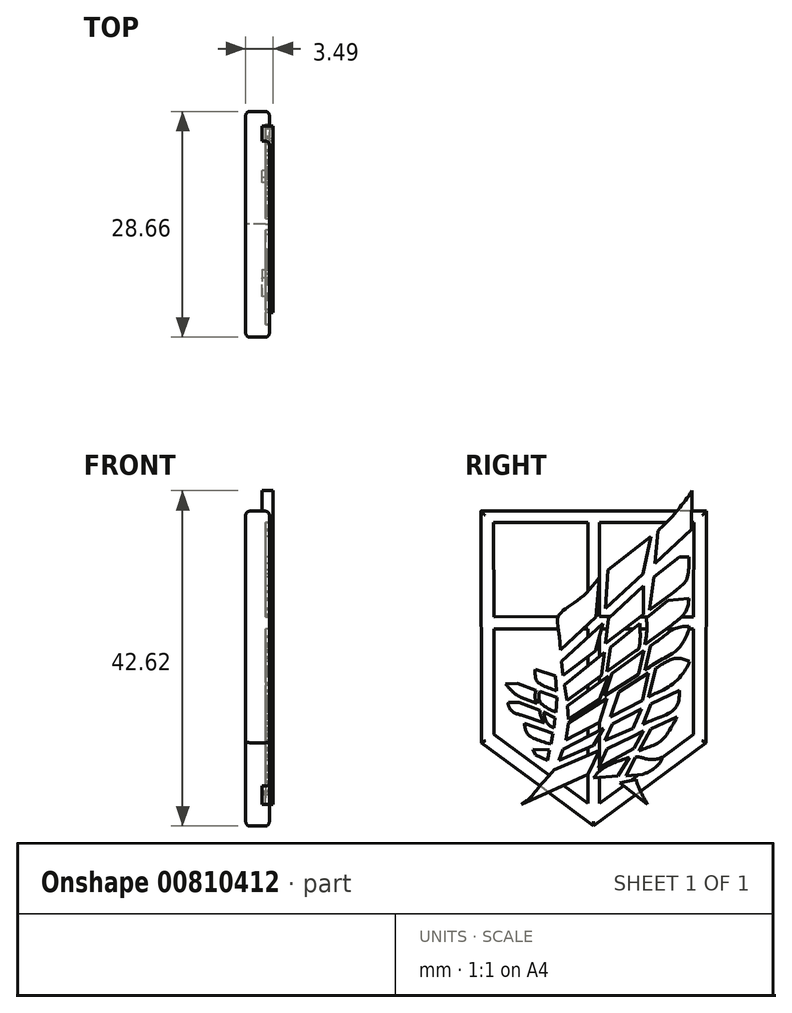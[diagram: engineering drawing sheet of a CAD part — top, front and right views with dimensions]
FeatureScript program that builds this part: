
annotation { "Feature Type Name" : "Feature", "Feature Type Description" : "" }
export const myFeature = defineFeature(function(context is Context, id is Id, definition is map)
    precondition{}
    {
        {
            var Q0;
            Q0=qCreatedBy(makeId("Right.planeOp"),FACE);
            var sketch = newSketch(context, id + "F0", { "sketchPlane" : qUnion([Q0])});
            skLineSegment(sketch, "E0.top", {"start": v(14.33, 19.11) * mm, "end": v(-14.33, 19.11) * mm});
            skPoint(sketch, "E0.middle", {"position": v(0, 0) * mm});
            skLineSegment(sketch, "E1", {"start": v(0, -20.89) * mm, "end": v(-14.26, -10.3) * mm});
            skLineSegment(sketch, "E2", {"start": v(0, 19.11) * mm, "end": v(0, -20.89) * mm, "construction": true});
            skLineSegment(sketch, "E3.MirrorCS", {"start": v(0, -20.89) * mm, "end": v(14.26, -10.3) * mm});
            skLineSegment(sketch, "E4", {"start": v(-14.33, 19.11) * mm, "end": v(-14.26, -10.3) * mm});
            skLineSegment(sketch, "E5", {"start": v(14.33, 19.11) * mm, "end": v(14.26, -10.3) * mm});
            skSolve(sketch);
        }
        {
            var Q0;
            Q0 = qSketchRegion(id + "F0", true);
            extrude(context, id + "F1", {"entities" : qUnion([Q0]), "depth" : 3 * mm, "offsetDistance" : 25 * mm});
        }
        {
            var Q0;
            Q0=makeQuery(id+"F1.opExtrude","CAP_EDGE",EDGE,{"disambiguationData":[OSD([sQuery(id+"F0.wireOp",EDGE,"E4")])],"isStart":false});
            var Q1;
            Q1=makeQuery(id+"F1.opExtrude","CAP_EDGE",EDGE,{"disambiguationData":[OSD([sQuery(id+"F0.wireOp",EDGE,"E0.top")])],"isStart":false});
            var Q2;
            Q2=makeQuery(id+"F1.opExtrude","CAP_EDGE",EDGE,{"disambiguationData":[OSD([sQuery(id+"F0.wireOp",EDGE,"E5")])],"isStart":false});
            var Q3;
            Q3=makeQuery(id+"F1.opExtrude","CAP_EDGE",EDGE,{"disambiguationData":[OSD([sQuery(id+"F0.wireOp",EDGE,"E3.MirrorCS")])],"isStart":false});
            var Q4;
            Q4=makeQuery(id+"F1.opExtrude","CAP_EDGE",EDGE,{"disambiguationData":[OSD([sQuery(id+"F0.wireOp",EDGE,"E1")])],"isStart":false});
            fillet(context, id + "F2", {"entities" : qUnion([Q0, Q1, Q2, Q3, Q4]), "radius" : 0.5 * mm, "tangentPropagation" : true, "allowEdgeOverflow" : false});
        }
        {
            var Q0;
            Q0=makeQuery(id+"F1.opExtrude","CAP_EDGE",EDGE,{"disambiguationData":[OSD([sQuery(id+"F0.wireOp",EDGE,"E5")])],"isStart":true});
            var Q1;
            Q1=makeQuery(id+"F1.opExtrude","CAP_EDGE",EDGE,{"disambiguationData":[OSD([sQuery(id+"F0.wireOp",EDGE,"E3.MirrorCS")])],"isStart":true});
            var Q2;
            Q2=makeQuery(id+"F1.opExtrude","CAP_EDGE",EDGE,{"disambiguationData":[OSD([sQuery(id+"F0.wireOp",EDGE,"E1")])],"isStart":true});
            var Q3;
            Q3=makeQuery(id+"F1.opExtrude","CAP_EDGE",EDGE,{"disambiguationData":[OSD([sQuery(id+"F0.wireOp",EDGE,"E4")])],"isStart":true});
            var Q4;
            Q4=makeQuery(id+"F1.opExtrude","CAP_EDGE",EDGE,{"disambiguationData":[OSD([sQuery(id+"F0.wireOp",EDGE,"E0.top")])],"isStart":true});
            fillet(context, id + "F3", {"entities" : qUnion([Q0, Q1, Q2, Q3, Q4]), "radius" : 0.5 * mm, "tangentPropagation" : true, "allowEdgeOverflow" : false});
        }
        {
            var Q0;
            Q0=makeQuery(id+"F1.opExtrude","CAP_FACE",FACE,{"disambiguationData":[OSD([sQuery(id+"F0.wireOp",EDGE,"E0.top"),sQuery(id+"F0.wireOp",EDGE,"E1"),sQuery(id+"F0.wireOp",EDGE,"E3.MirrorCS"),sQuery(id+"F0.wireOp",EDGE,"E4"),sQuery(id+"F0.wireOp",EDGE,"E5")])],"isStart":false});
            var sketch = newSketch(context, id + "F4", { "sketchPlane" : qUnion([Q0])});
            skLineSegment(sketch, "E6", {"start": v(0, 18.61) * mm, "end": v(-13.83, 18.61) * mm});
            skLineSegment(sketch, "E7", {"start": v(-13.83, 18.61) * mm, "end": v(-13.76, -10.04) * mm});
            skLineSegment(sketch, "E8", {"start": v(-13.76, -10.04) * mm, "end": v(0, -20.27) * mm});
            skLineSegment(sketch, "E9", {"start": v(0, -20.27) * mm, "end": v(13.76, -10.04) * mm});
            skLineSegment(sketch, "E10", {"start": v(13.76, -10.04) * mm, "end": v(13.83, 18.61) * mm});
            skLineSegment(sketch, "E11", {"start": v(13.83, 18.61) * mm, "end": v(0, 18.61) * mm});
            skLineSegment(sketch, "E12", {"start": v(0, 18.61) * mm, "end": v(0, -20.27) * mm});
            skLineSegment(sketch, "E13", {"start": v(-12.7, 4.17) * mm, "end": v(-12.7, -9.22) * mm});
            skLineSegment(sketch, "E14", {"start": v(-12.7, -9.22) * mm, "end": v(-0.75, -18.02) * mm});
            skLineSegment(sketch, "E15", {"start": v(-0.75, -18.02) * mm, "end": v(-0.75, 4.17) * mm});
            skLineSegment(sketch, "E16", {"start": v(-0.75, 4.17) * mm, "end": v(-12.7, 4.17) * mm});
            skLineSegment(sketch, "E17", {"start": v(-12.75, 17.67) * mm, "end": v(-12.7, 5.67) * mm});
            skLineSegment(sketch, "E18", {"start": v(-12.7, 5.67) * mm, "end": v(-0.76, 5.73) * mm});
            skLineSegment(sketch, "E19", {"start": v(-0.76, 5.73) * mm, "end": v(-0.75, 17.7) * mm});
            skLineSegment(sketch, "E20", {"start": v(-0.75, 17.7) * mm, "end": v(-12.75, 17.67) * mm});
            skLineSegment(sketch, "E21.MirrorCS", {"start": v(0.76, 5.73) * mm, "end": v(0.75, 17.7) * mm});
            skLineSegment(sketch, "E22.MirrorCS", {"start": v(0.75, 17.7) * mm, "end": v(12.75, 17.67) * mm});
            skLineSegment(sketch, "E23.MirrorCS", {"start": v(12.75, 17.67) * mm, "end": v(12.7, 5.67) * mm});
            skLineSegment(sketch, "E24.MirrorCS", {"start": v(12.7, 5.67) * mm, "end": v(0.76, 5.73) * mm});
            skLineSegment(sketch, "E25.MirrorCS", {"start": v(0.75, -18.02) * mm, "end": v(0.75, 4.17) * mm});
            skLineSegment(sketch, "E26.MirrorCS", {"start": v(0.75, 4.17) * mm, "end": v(12.7, 4.17) * mm});
            skLineSegment(sketch, "E27.MirrorCS", {"start": v(12.7, -9.22) * mm, "end": v(0.75, -18.02) * mm});
            skLineSegment(sketch, "E28.MirrorCS", {"start": v(12.7, 4.17) * mm, "end": v(12.7, -9.22) * mm});
            skSolve(sketch);
        }
        {
            var Q0;
            Q0=makeQuery(id+"F4.imprint","IMPRINT",FACE,{"disambiguationData":[TD([[makeQuery(id+"F4.imprint","IMPRINT",EDGE,{"derivedFrom":sQuery(id+"F4.wireOp",EDGE,"E17")}),1.0]])]});
            var Q1;
            Q1=makeQuery(id+"F4.imprint","IMPRINT",FACE,{"disambiguationData":[TD([[makeQuery(id+"F4.imprint","IMPRINT",EDGE,{"derivedFrom":sQuery(id+"F4.wireOp",EDGE,"E13")}),1.0]])]});
            var Q2;
            Q2=makeQuery(id+"F4.imprint","IMPRINT",FACE,{"disambiguationData":[TD([[makeQuery(id+"F4.imprint","IMPRINT",EDGE,{"derivedFrom":sQuery(id+"F4.wireOp",EDGE,"E21.MirrorCS")}),-1.0]])]});
            var Q3;
            Q3=makeQuery(id+"F4.imprint","IMPRINT",FACE,{"disambiguationData":[TD([[makeQuery(id+"F4.imprint","IMPRINT",EDGE,{"derivedFrom":sQuery(id+"F4.wireOp",EDGE,"E25.MirrorCS")}),-1.0]])]});
            extrude(context, id + "F5", {"entities" : qUnion([Q0, Q1, Q2, Q3]), "operationType" : NewBodyOperationType.REMOVE, "oppositeDirection" : true, "depth" : 0.49 * mm, "offsetDistance" : 25 * mm});
        }
        {
            var Q0;
            Q0=makeQuery(id+"F1.opExtrude","CAP_FACE",FACE,{"disambiguationData":[OSD([sQuery(id+"F0.wireOp",EDGE,"E0.top"),sQuery(id+"F0.wireOp",EDGE,"E1"),sQuery(id+"F0.wireOp",EDGE,"E3.MirrorCS"),sQuery(id+"F0.wireOp",EDGE,"E4"),sQuery(id+"F0.wireOp",EDGE,"E5")])],"isStart":false});
            var sketch = newSketch(context, id + "F6", { "sketchPlane" : qUnion([Q0])});
            skLineSegment(sketch, "E29", {"start": v(-0.75, -14.35) * mm, "end": v(-9.17, -18.12) * mm});
            skFitSpline(sketch, "E30", {"points": [v(-9.17, -18.12) * mm, v(-8.07, -17.3) * mm, v(-6.52, -15.42) * mm, v(-5.07, -13.75) * mm], "startDerivative": vector(5.46, 4.28) * mm, "endDerivative": vector(4.45, 5.93) * mm});
            skPoint(sketch, "E31", {"position": v(-7.12, -16.16) * mm});
            skLineSegment(sketch, "E32", {"start": v(-0.75, -14.35) * mm, "end": v(0.75, -11.27) * mm});
            skLineSegment(sketch, "E33", {"start": v(0.75, -11.27) * mm, "end": v(-5.07, -13.75) * mm});
            skLineSegment(sketch, "E34", {"start": v(0.6, -13.5) * mm, "end": v(1.69, -11.1) * mm});
            skLineSegment(sketch, "E35", {"start": v(1.69, -11.1) * mm, "end": v(4.98, -9.52) * mm});
            skLineSegment(sketch, "E36", {"start": v(0.6, -13.5) * mm, "end": v(5.09, -11.04) * mm});
            skLineSegment(sketch, "E37", {"start": v(5.09, -11.04) * mm, "end": v(6.3, -8.8) * mm});
            skLineSegment(sketch, "E38", {"start": v(6.3, -8.8) * mm, "end": v(4.98, -9.52) * mm});
            skLineSegment(sketch, "E39", {"start": v(7.29, -8.53) * mm, "end": v(5.77, -11.32) * mm});
            skLineSegment(sketch, "E40", {"start": v(7.29, -8.53) * mm, "end": v(10.58, -7.01) * mm});
            skFitSpline(sketch, "E41", {"points": [v(5.77, -11.32) * mm, v(8.5, -10.1) * mm, v(10.58, -7.01) * mm], "startDerivative": vector(6.29, 2.79) * mm, "endDerivative": vector(3.58, 6.64) * mm});
            skLineSegment(sketch, "E42", {"start": v(0, -14.79) * mm, "end": v(3.1, -14.5) * mm});
            skLineSegment(sketch, "E43", {"start": v(3.1, -14.5) * mm, "end": v(4.52, -12.17) * mm});
            skPoint(sketch, "E44.3.internal.snap0", {"position": v(2.84, -12.27) * mm});
            skPoint(sketch, "E45", {"position": v(2.26, -13.48) * mm});
            skFitSpline(sketch, "E46", {"points": [v(0, -14.79) * mm, v(0.75, -13.9) * mm, v(2.26, -13) * mm, v(4.52, -12.17) * mm], "startDerivative": vector(2.4, 3.4) * mm, "endDerivative": vector(5.99, 1.99) * mm});
            skPoint(sketch, "E47.1.internal.snap0", {"position": v(3.8, -13.34) * mm});
            skLineSegment(sketch, "E48", {"start": v(4.1, -14.5) * mm, "end": v(5.28, -12.14) * mm});
            skPoint(sketch, "E49.1.internal.snap0", {"position": v(6.72, -13.62) * mm});
            skPoint(sketch, "E49.4.internal.snap0", {"position": v(6.88, -15.15) * mm});
            skFitSpline(sketch, "E50", {"points": [v(5.28, -12.14) * mm, v(5.89, -12.14) * mm, v(6.64, -12.36) * mm, v(7.91, -12.4) * mm, v(8.73, -12.14) * mm], "startDerivative": vector(2.9, 0.26) * mm, "endDerivative": vector(3, 1.23) * mm});
            skFitSpline(sketch, "E51", {"points": [v(8.73, -12.14) * mm, v(8.48, -12.72) * mm, v(7.74, -13.52) * mm, v(6.7, -14.14) * mm, v(6.23, -14.3) * mm], "startDerivative": vector(-0.9, -2.6) * mm, "endDerivative": vector(-2.16, -0.6) * mm});
            skLineSegment(sketch, "E52", {"start": v(4.1, -14.5) * mm, "end": v(6.23, -14.3) * mm});
            skLineSegment(sketch, "E53", {"start": v(5.4, -14.99) * mm, "end": v(3.31, -15.42) * mm});
            skPoint(sketch, "E54.2.internal.snap0", {"position": v(4.36, -15.2) * mm});
            skLineSegment(sketch, "E55", {"start": v(-9.17, -18.12) * mm, "end": v(11.05, -18.12) * mm, "construction": true});
            skLineSegment(sketch, "E56", {"start": v(3.31, -15.42) * mm, "end": v(6.85, -18.12) * mm});
            skFitSpline(sketch, "E57", {"points": [v(5.4, -14.99) * mm, v(5.48, -15.29) * mm, v(5.67, -15.83) * mm, v(5.93, -16.46) * mm, v(6.16, -16.9) * mm, v(6.6, -17.69) * mm, v(6.85, -18.12) * mm], "startDerivative": vector(0.75, -2.31) * mm, "endDerivative": vector(1.42, -2.48) * mm});
            skFitSpline(sketch, "E58", {"points": [v(-5.07, -13.75) * mm, v(-4.19, -11.96) * mm, v(-3.23, -7.81) * mm, v(-4, -0.95) * mm, v(-4.64, 5.71) * mm], "startDerivative": vector(5.68, 9.91) * mm, "endDerivative": vector(-3.76, 21.86) * mm, "construction": true});
            skLineSegment(sketch, "E59", {"start": v(-3.88, -11.13) * mm, "end": v(-4.44, -12.54) * mm});
            skFitSpline(sketch, "E60", {"points": [v(-4.64, 5.71) * mm, v(-4.64, 6.7) * mm, v(-2.24, 8.4) * mm, v(2.56, 12.25) * mm, v(9.26, 17.68) * mm, v(12.46, 21.73) * mm, v(12.48, 21.9) * mm], "startDerivative": vector(-2.87, 11.45) * mm, "endDerivative": vector(-0.94, 2.56) * mm, "construction": true});
            skFitSpline(sketch, "E61", {"points": [v(10.58, -7.01) * mm, v(11.67, -2.07) * mm, v(13.34, 6.4) * mm, v(12.46, 21.73) * mm], "startDerivative": vector(3.82, 19.04) * mm, "endDerivative": vector(-4.27, 37.96) * mm, "construction": true});
            skPoint(sketch, "E62.0.internal.snap0", {"position": v(-6.72, -13.62) * mm});
            skPoint(sketch, "E62.2.internal.snap0", {"position": v(-4.96, -16.24) * mm});
            skPoint(sketch, "E62.3.internal.snap0", {"position": v(-4.96, -16.24) * mm});
            skPoint(sketch, "E62.4.internal.snap0", {"position": v(-6.72, -13.62) * mm});
            skFitSpline(sketch, "E62", {"points": [v(-6.15, -13.62) * mm, v(-5.6, -11.2) * mm, v(-4.96, -7.66) * mm, v(-4.96, -1.26) * mm, v(-6.72, 5.7) * mm, v(-5.6, 7.98) * mm, v(-1.64, 10.32) * mm], "startDerivative": vector(5.06, 18.87) * mm, "endDerivative": vector(25.42, 13.57) * mm, "construction": true});
            skFitSpline(sketch, "E63", {"points": [v(-11.36, 20.74) * mm, v(-8.65, 20.1) * mm, v(-2.94, 16) * mm, v(-1.64, 10.32) * mm], "startDerivative": vector(9.6, -1.22) * mm, "endDerivative": vector(0.23, -16.78) * mm, "construction": true});
            skFitSpline(sketch, "E64", {"points": [v(-12.28, 9.15) * mm, v(-12.72, 11.67) * mm, v(-12.73, 14.4) * mm, v(-11.36, 20.74) * mm], "startDerivative": vector(-1.84, 9.3) * mm, "endDerivative": vector(4.02, 15.96) * mm, "construction": true});
            skLineSegment(sketch, "E65", {"start": v(1.22, -8.5) * mm, "end": v(0, -10.63) * mm});
            skLineSegment(sketch, "E66", {"start": v(0, -10.63) * mm, "end": v(-4.44, -12.54) * mm});
            skLineSegment(sketch, "E67", {"start": v(-3.88, -11.13) * mm, "end": v(1.22, -8.5) * mm});
            skLineSegment(sketch, "E68", {"start": v(1.43, -10.02) * mm, "end": v(2.38, -7.92) * mm});
            skLineSegment(sketch, "E69", {"start": v(2.38, -7.92) * mm, "end": v(6.1, -6) * mm});
            skLineSegment(sketch, "E70", {"start": v(6.1, -6) * mm, "end": v(4.97, -8.5) * mm});
            skLineSegment(sketch, "E71", {"start": v(4.97, -8.5) * mm, "end": v(1.43, -10.02) * mm});
            skLineSegment(sketch, "E72", {"start": v(7.3, -5.39) * mm, "end": v(6.24, -7.96) * mm});
            skFitSpline(sketch, "E73", {"points": [v(6.24, -7.96) * mm, v(7.73, -7.31) * mm, v(9.8, -6.43) * mm, v(10.68, -5.37) * mm, v(10.9, -3.66) * mm], "startDerivative": vector(5.71, 2.62) * mm, "endDerivative": vector(0.28, 7.35) * mm});
            skFitSpline(sketch, "E74", {"points": [v(7.3, -5.39) * mm, v(10.9, -3.66) * mm], "startDerivative": vector(3.6, 1.73) * mm, "endDerivative": vector(3.6, 1.73) * mm});
            skLineSegment(sketch, "E75", {"start": v(-3.53, -9.95) * mm, "end": v(-3.23, -7.81) * mm});
            skLineSegment(sketch, "E76", {"start": v(1.71, -4.7) * mm, "end": v(0.75, -7.73) * mm});
            skPoint(sketch, "E76.endSnap0", {"position": v(0.75, -6.92) * mm});
            skLineSegment(sketch, "E77", {"start": v(0.75, -7.73) * mm, "end": v(-3.53, -9.95) * mm});
            skLineSegment(sketch, "E78", {"start": v(-3.23, -7.81) * mm, "end": v(1.71, -4.7) * mm});
            skLineSegment(sketch, "E79", {"start": v(2.15, -7) * mm, "end": v(3.2, -3.86) * mm});
            skPoint(sketch, "E79.endSnap0", {"position": v(3.2, -9.26) * mm});
            skLineSegment(sketch, "E80", {"start": v(3.2, -3.86) * mm, "end": v(6.94, -1.45) * mm});
            skLineSegment(sketch, "E81", {"start": v(6.94, -1.45) * mm, "end": v(6.2, -4.9) * mm});
            skLineSegment(sketch, "E82", {"start": v(6.2, -4.9) * mm, "end": v(2.15, -7) * mm});
            skLineSegment(sketch, "E83", {"start": v(7.94, -0.83) * mm, "end": v(6.94, -4.52) * mm});
            skFitSpline(sketch, "E84", {"points": [v(6.94, -4.52) * mm, v(7.98, -3.98) * mm, v(9.72, -3.08) * mm, v(11.43, -1.35) * mm, v(12.2, 0) * mm], "startDerivative": vector(4.71, 2.6) * mm, "endDerivative": vector(2.67, 5.56) * mm});
            skFitSpline(sketch, "E85", {"points": [v(7.94, -0.83) * mm, v(9.26, 0) * mm, v(10.77, 0.43) * mm, v(12.2, 0) * mm], "startDerivative": vector(3.8, 2.6) * mm, "endDerivative": vector(4.26, -1.94) * mm});
            skLineSegment(sketch, "E86", {"start": v(0.75, -4.8) * mm, "end": v(1.9, -1.82) * mm});
            skLineSegment(sketch, "E87", {"start": v(-3.34, -5.6) * mm, "end": v(1.9, -1.82) * mm});
            skLineSegment(sketch, "E88", {"start": v(-3.34, -5.6) * mm, "end": v(-3.23, -7.35) * mm});
            skLineSegment(sketch, "E89", {"start": v(1.39, -4.38) * mm, "end": v(2.34, -1.5) * mm});
            skLineSegment(sketch, "E90", {"start": v(6.42, 1.43) * mm, "end": v(5.7, -1.6) * mm});
            skLineSegment(sketch, "E91", {"start": v(1.39, -4.38) * mm, "end": v(5.7, -1.6) * mm});
            skLineSegment(sketch, "E92", {"start": v(2.34, -1.5) * mm, "end": v(6.42, 1.43) * mm});
            skLineSegment(sketch, "E93", {"start": v(6.5, -1.09) * mm, "end": v(7.23, 2.01) * mm});
            skFitSpline(sketch, "E94", {"points": [v(6.5, -1.09) * mm, v(8.62, 0.28) * mm, v(10.78, 1.67) * mm, v(12.11, 4.17) * mm, v(12.11, 4.52) * mm], "startDerivative": vector(7.17, 5.06) * mm, "endDerivative": vector(-0.5, 2.4) * mm});
            skFitSpline(sketch, "E95", {"points": [v(7.23, 2.01) * mm, v(9.02, 3.3) * mm, v(10.24, 4.17) * mm, v(12.11, 4.52) * mm], "startDerivative": vector(5.28, 3.6) * mm, "endDerivative": vector(6.03, 0.55) * mm});
            skLineSegment(sketch, "E96", {"start": v(-3.43, -4.9) * mm, "end": v(-3.72, -2.98) * mm});
            skLineSegment(sketch, "E97", {"start": v(-3.72, -2.98) * mm, "end": v(1.37, 1.18) * mm});
            skLineSegment(sketch, "E98", {"start": v(1.37, 1.18) * mm, "end": v(1, -1.75) * mm});
            skLineSegment(sketch, "E99", {"start": v(1, -1.75) * mm, "end": v(-3.43, -4.9) * mm});
            skLineSegment(sketch, "E100", {"start": v(1.68, -1.26) * mm, "end": v(2.15, 1.83) * mm});
            skLineSegment(sketch, "E101", {"start": v(-3.23, -7.35) * mm, "end": v(0.75, -4.8) * mm});
            skLineSegment(sketch, "E102", {"start": v(1.68, -1.26) * mm, "end": v(5.33, 1.37) * mm});
            skLineSegment(sketch, "E103", {"start": v(5.86, 4.85) * mm, "end": v(2.15, 1.83) * mm});
            skFitSpline(sketch, "E104", {"points": [v(5.33, 1.37) * mm, v(5.65, 1.6) * mm, v(5.9, 2.5) * mm, v(5.86, 4.85) * mm], "startDerivative": vector(1.73, 0.85) * mm, "endDerivative": vector(-0.25, 5.22) * mm});
            skPoint(sketch, "E105.2.internal.snap0", {"position": v(6.72, 4.17) * mm});
            skFitSpline(sketch, "E105", {"points": [v(6.7, 5.53) * mm, v(6.75, 4.85) * mm, v(6.72, 3.62) * mm, v(6.51, 2.22) * mm], "startDerivative": vector(0.24, -2.38) * mm, "endDerivative": vector(-0.65, -3.67) * mm});
            skLineSegment(sketch, "E106", {"start": v(6.51, 2.22) * mm, "end": v(9.95, 4.69) * mm});
            skLineSegment(sketch, "E107", {"start": v(6.7, 5.53) * mm, "end": v(9.46, 7.78) * mm});
            skLineSegment(sketch, "E108", {"start": v(9.46, 7.78) * mm, "end": v(12.11, 8.05) * mm});
            skFitSpline(sketch, "E109", {"points": [v(9.95, 4.69) * mm, v(10.92, 5.48) * mm, v(11.8, 6.55) * mm, v(12.11, 8.05) * mm], "startDerivative": vector(3.08, 2.38) * mm, "endDerivative": vector(0.46, 4.53) * mm});
            skLineSegment(sketch, "E110", {"start": v(-3.9, -1.75) * mm, "end": v(13.4, 11.32) * mm, "construction": true});
            skLineSegment(sketch, "E111", {"start": v(-4.1, 0) * mm, "end": v(13.09, 15.8) * mm, "construction": true});
            skLineSegment(sketch, "E112", {"start": v(-3.9, -1.75) * mm, "end": v(-4.1, 0) * mm});
            skLineSegment(sketch, "E113", {"start": v(-3.9, -1.75) * mm, "end": v(0.23, 1.37) * mm});
            skLineSegment(sketch, "E114", {"start": v(0.23, 1.37) * mm, "end": v(1.18, 4.86) * mm});
            skLineSegment(sketch, "E115", {"start": v(1.18, 4.86) * mm, "end": v(-4.1, 0) * mm});
            skLineSegment(sketch, "E116", {"start": v(1.48, 2.31) * mm, "end": v(1.89, 5.5) * mm});
            skLineSegment(sketch, "E117", {"start": v(1.48, 2.31) * mm, "end": v(6.32, 5.97) * mm});
            skLineSegment(sketch, "E118", {"start": v(6.32, 5.97) * mm, "end": v(6.32, 9.59) * mm});
            skLineSegment(sketch, "E119", {"start": v(6.32, 9.59) * mm, "end": v(1.89, 5.5) * mm});
            skLineSegment(sketch, "E120", {"start": v(7.63, 10.79) * mm, "end": v(7.1, 6.56) * mm});
            skLineSegment(sketch, "E121", {"start": v(7.1, 6.56) * mm, "end": v(10.13, 8.8) * mm});
            skLineSegment(sketch, "E122", {"start": v(12.09, 13.3) * mm, "end": v(10.87, 13.3) * mm});
            skLineSegment(sketch, "E123", {"start": v(10.87, 13.3) * mm, "end": v(7.63, 10.79) * mm});
            skFitSpline(sketch, "E124", {"points": [v(10.13, 8.8) * mm, v(10.98, 9.48) * mm, v(11.88, 10.62) * mm, v(12.09, 13.3) * mm], "startDerivative": vector(2.81, 2.17) * mm, "endDerivative": vector(-0.03, 5) * mm});
            skLineSegment(sketch, "E125", {"start": v(-4.23, 1.52) * mm, "end": v(12.75, 17.07) * mm, "construction": true});
            skLineSegment(sketch, "E126", {"start": v(12.75, 17.07) * mm, "end": v(12.95, 17.25) * mm, "construction": true});
            skLineSegment(sketch, "E127", {"start": v(-4.23, 1.52) * mm, "end": v(-4.35, 3.23) * mm});
            skLineSegment(sketch, "E128", {"start": v(0.75, 10.75) * mm, "end": v(0.29, 5.65) * mm});
            skLineSegment(sketch, "E129", {"start": v(0.29, 5.65) * mm, "end": v(-4.23, 1.52) * mm});
            skLineSegment(sketch, "E130", {"start": v(1.5, 6.76) * mm, "end": v(1.83, 11.65) * mm});
            skLineSegment(sketch, "E131", {"start": v(1.83, 11.65) * mm, "end": v(7.26, 15.87) * mm});
            skLineSegment(sketch, "E132", {"start": v(7.26, 15.87) * mm, "end": v(6.26, 11.12) * mm});
            skLineSegment(sketch, "E133", {"start": v(6.26, 11.12) * mm, "end": v(1.5, 6.76) * mm});
            skLineSegment(sketch, "E134", {"start": v(7.77, 12.5) * mm, "end": v(8.14, 16.63) * mm});
            skLineSegment(sketch, "E135", {"start": v(12.46, 21.73) * mm, "end": v(12.44, 16.79) * mm});
            skLineSegment(sketch, "E136", {"start": v(12.44, 16.79) * mm, "end": v(7.77, 12.5) * mm});
            skFitSpline(sketch, "E137", {"points": [v(8.14, 16.63) * mm, v(8.62, 17.07) * mm, v(9.72, 18.17) * mm, v(10.97, 19.6) * mm, v(12.05, 21.05) * mm, v(12.32, 21.47) * mm, v(12.46, 21.73) * mm], "startDerivative": vector(3.18, 2.94) * mm, "endDerivative": vector(1.49, 3.04) * mm});
            skFitSpline(sketch, "E138", {"points": [v(-4.35, 3.23) * mm, v(-4.6, 5.41) * mm, v(-4.35, 6.03) * mm, v(-3.42, 6.83) * mm, v(-1.22, 8.44) * mm, v(0.75, 10.75) * mm], "startDerivative": vector(-0.98, 4.12) * mm, "endDerivative": vector(6.62, 7.59) * mm});
            skLineSegment(sketch, "E139", {"start": v(-5.6, -11.2) * mm, "end": v(-5.6, -11.2) * mm});
            skLineSegment(sketch, "E140", {"start": v(-5.6, -11.2) * mm, "end": v(-7.7, -11.13) * mm});
            skLineSegment(sketch, "E141", {"start": v(-7.7, -11.13) * mm, "end": v(-7.4, -11.84) * mm});
            skLineSegment(sketch, "E142", {"start": v(-7.4, -11.84) * mm, "end": v(-5.89, -12.55) * mm});
            skLineSegment(sketch, "E143", {"start": v(-5.89, -12.55) * mm, "end": v(-5.6, -11.2) * mm});
            skLineSegment(sketch, "E144", {"start": v(-5.45, -10.47) * mm, "end": v(-5.19, -9.09) * mm});
            skLineSegment(sketch, "E145", {"start": v(-5.19, -9.09) * mm, "end": v(-8.81, -7.86) * mm});
            skLineSegment(sketch, "E146", {"start": v(-5.08, -8.42) * mm, "end": v(-4.9, -7.14) * mm});
            skLineSegment(sketch, "E147", {"start": v(-4.9, -7.14) * mm, "end": v(-6.36, -6.36) * mm});
            skLineSegment(sketch, "E148", {"start": v(-6.82, -6.2) * mm, "end": v(-9.49, -5.2) * mm});
            skFitSpline(sketch, "E149", {"points": [v(-8.81, -7.86) * mm, v(-8.64, -8.61) * mm, v(-8.18, -9.39) * mm, v(-5.45, -10.47) * mm], "startDerivative": vector(0.6, -3.04) * mm, "endDerivative": vector(6.9, -2.03) * mm});
            skLineSegment(sketch, "E150", {"start": v(-6.27, -7.78) * mm, "end": v(-9.06, -6.83) * mm});
            skLineSegment(sketch, "E151", {"start": v(-9.71, -5.2) * mm, "end": v(-9.49, -5.2) * mm});
            skFitSpline(sketch, "E152", {"points": [v(-6.36, -6.36) * mm, v(-6.27, -6.86) * mm, v(-6.11, -7.39) * mm, v(-5.79, -7.94) * mm, v(-5.08, -8.42) * mm], "startDerivative": vector(0.37, -2.22) * mm, "endDerivative": vector(2.7, -1.5) * mm});
            skFitSpline(sketch, "E153", {"points": [v(-6.82, -6.2) * mm, v(-6.82, -6.49) * mm, v(-6.74, -6.89) * mm, v(-6.47, -7.52) * mm, v(-6.27, -7.78) * mm], "startDerivative": vector(-0.03, -1.32) * mm, "endDerivative": vector(0.35, -1.17) * mm});
            skLineSegment(sketch, "E154", {"start": v(-4.8, -6.45) * mm, "end": v(-4.69, -4.52) * mm});
            skLineSegment(sketch, "E155", {"start": v(-4.69, -4.52) * mm, "end": v(-6.85, -3.77) * mm});
            skFitSpline(sketch, "E156", {"points": [v(-6.85, -3.77) * mm, v(-6.85, -5.04) * mm, v(-4.8, -6.45) * mm], "startDerivative": vector(-0.55, -2.04) * mm, "endDerivative": vector(4.2, -2.2) * mm});
            skFitSpline(sketch, "E157", {"points": [v(-7.2, -5.32) * mm, v(-7.43, -4.75) * mm, v(-7.45, -4.2) * mm, v(-7.32, -3.68) * mm], "startDerivative": vector(-0.77, 1.64) * mm, "endDerivative": vector(0.46, 1.57) * mm});
            skLineSegment(sketch, "E158", {"start": v(-7.32, -3.68) * mm, "end": v(-9.7, -2.76) * mm});
            skLineSegment(sketch, "E159", {"start": v(-7.2, -5.32) * mm, "end": v(-9.27, -4.52) * mm});
            skLineSegment(sketch, "E160", {"start": v(-11.19, -2.81) * mm, "end": v(-9.7, -2.76) * mm});
            skFitSpline(sketch, "E161", {"points": [v(-9.27, -4.52) * mm, v(-9.48, -4.41) * mm, v(-9.82, -4.2) * mm, v(-10.51, -3.63) * mm, v(-11.19, -2.81) * mm], "startDerivative": vector(-0.86, 0.92) * mm, "endDerivative": vector(-1.6, 2) * mm});
            skLineSegment(sketch, "E162", {"start": v(-4.7, -3.72) * mm, "end": v(-4.87, -1.79) * mm});
            skLineSegment(sketch, "E163", {"start": v(-4.87, -1.79) * mm, "end": v(-7.42, -1) * mm});
            skFitSpline(sketch, "E164", {"points": [v(-7.42, -1) * mm, v(-7.42, -1.75) * mm, v(-7.13, -2.55) * mm, v(-4.7, -3.72) * mm], "startDerivative": vector(-0.1, -2.95) * mm, "endDerivative": vector(6.35, -2.24) * mm});
            skLineSegment(sketch, "E165", {"start": v(-9.71, -5.2) * mm, "end": v(-10.85, -5.2) * mm});
            skFitSpline(sketch, "E166", {"points": [v(-10.85, -5.2) * mm, v(-10.85, -5.5) * mm, v(-10.4, -6.26) * mm, v(-9.06, -6.83) * mm], "startDerivative": vector(-0.18, -1.3) * mm, "endDerivative": vector(3.41, -0.93) * mm});
            skSolve(sketch);
        }
        {
            var Q0;
            Q0 = qSketchRegion(id + "F6", true);
            extrude(context, id + "F7", {"entities" : qUnion([Q0]), "operationType" : NewBodyOperationType.ADD, "depth" : 0.49 * mm, "offsetDistance" : 25 * mm, "hasSecondDirection" : true, "secondDirectionOppositeDirection" : true, "secondDirectionDepth" : 0.9 * mm});
        }
    });
